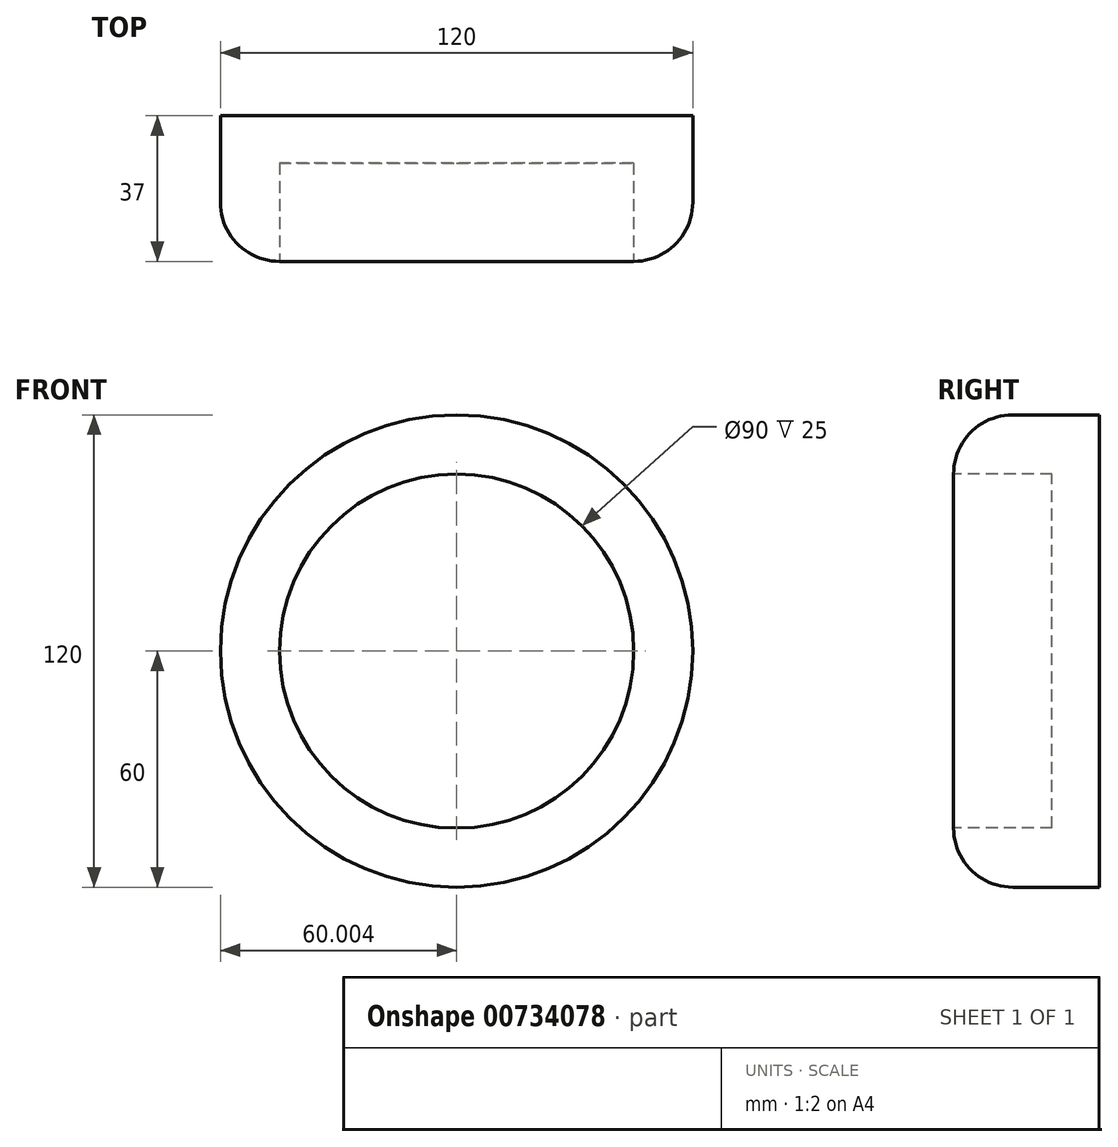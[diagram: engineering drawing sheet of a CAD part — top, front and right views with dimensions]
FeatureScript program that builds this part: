
annotation { "Feature Type Name" : "Feature", "Feature Type Description" : "" }
export const myFeature = defineFeature(function(context is Context, id is Id, definition is map)
    precondition{}
    {
        {
            var Q0;
            Q0=qCreatedBy(makeId("Front.planeOp"),FACE);
            var sketch = newSketch(context, id + "F0", { "sketchPlane" : qUnion([Q0])});
            skCircle(sketch, "E0", {"center": v(20.5, 3.3) * mm, "radius": 60 * mm});
            skSolve(sketch);
        }
        {
            var Q0;
            Q0 = qSketchRegion(id + "F0", true);
            extrude(context, id + "F1", {"entities" : qUnion([Q0]), "depth" : 25 * mm, "offsetDistance" : 25 * mm});
        }
        {
            var Q0;
            Q0=makeQuery(id+"F1.opExtrude","CAP_FACE",FACE,{"disambiguationData":[OSD([sQuery(id+"F0.wireOp",EDGE,"E0")])],"isStart":false});
            var Q1;
            Q1=makeQuery(id+"F1.opExtrude","CAP_FACE",FACE,{"disambiguationData":[OSD([sQuery(id+"F0.wireOp",EDGE,"E0")])],"isStart":true});
            extrude(context, id + "F2", {"entities" : qUnion([Q0, Q1]), "operationType" : NewBodyOperationType.ADD, "depth" : 25 * mm, "offsetDistance" : 25 * mm});
        }
        {
            var Q0;
            {var subQ0=sQuery(id+"F0.wireOp",EDGE,"E0");Q0=makeQuery(id+"F2.opExtrude","CAP_FACE",FACE,{"disambiguationData":[OSD([subQ0]),TDD([makeQuery(id+"F1.opExtrude","CAP_FACE",FACE,{"disambiguationData":[OSD([subQ0])],"isStart":false})])],"isStart":false});}
            extrude(context, id + "F3", {"entities" : qUnion([Q0]), "operationType" : NewBodyOperationType.INTERSECT, "oppositeDirection" : true, "depth" : 37 * mm, "offsetDistance" : 25 * mm});
        }
        {
            var Q0;
            {var subQ0=sQuery(id+"F0.wireOp",EDGE,"E0");Q0=makeQuery(id+"F2.opExtrude","CAP_FACE",FACE,{"disambiguationData":[OSD([subQ0]),TDD([makeQuery(id+"F1.opExtrude","CAP_FACE",FACE,{"disambiguationData":[OSD([subQ0])],"isStart":false})])],"isStart":false});}
            fillet(context, id + "F4", {"entities" : qUnion([Q0]), "radius" : 15 * mm, "tangentPropagation" : true, "allowEdgeOverflow" : false});
        }
        {
            var Q0;
            {var subQ0=sQuery(id+"F0.wireOp",EDGE,"E0");Q0=makeQuery(id+"F2.opExtrude","CAP_FACE",FACE,{"disambiguationData":[OSD([subQ0]),TDD([makeQuery(id+"F1.opExtrude","CAP_FACE",FACE,{"disambiguationData":[OSD([subQ0])],"isStart":false})])],"isStart":false});}
            var sketch = newSketch(context, id + "F5", { "sketchPlane" : qUnion([Q0])});
            skSolve(sketch);
        }
        {
            var Q0;
            Q0 = qSketchRegion(id + "F5", true);
            var Q1;
            {var subQ0=sQuery(id+"F0.wireOp",EDGE,"E0");Q1=makeQuery(id+"F5.imprint","IMPRINT",FACE,{"disambiguationData":[TD([[makeQuery(id+"F5.imprint","IMPRINT",EDGE,{"derivedFrom":makeQuery(id+"F4.opFillet","BLEND_EDGE",EDGE,{"blendedFrom":[makeQuery(id+"F2.opExtrude","CAP_EDGE",EDGE,{"disambiguationData":[OSD([subQ0]),TDD([makeQuery(id+"F1.opExtrude","CAP_EDGE",EDGE,{"disambiguationData":[OSD([subQ0])],"isStart":false})])],"isStart":false}),makeQuery(id+"F2.opExtrude","CAP_FACE",FACE,{"disambiguationData":[OSD([subQ0]),TDD([makeQuery(id+"F1.opExtrude","CAP_FACE",FACE,{"disambiguationData":[OSD([subQ0])],"isStart":false})])],"isStart":false})],"blendedInto":[makeQuery(id+"F2.opExtrude","CAP_FACE",FACE,{"disambiguationData":[OSD([subQ0]),TDD([makeQuery(id+"F1.opExtrude","CAP_FACE",FACE,{"disambiguationData":[OSD([subQ0])],"isStart":false})])],"isStart":false})]})}),1.0]])]});}
            extrude(context, id + "F6", {"entities" : qUnion([Q0, Q1]), "operationType" : NewBodyOperationType.REMOVE, "oppositeDirection" : true, "depth" : 25 * mm, "offsetDistance" : 25 * mm});
        }
    });
